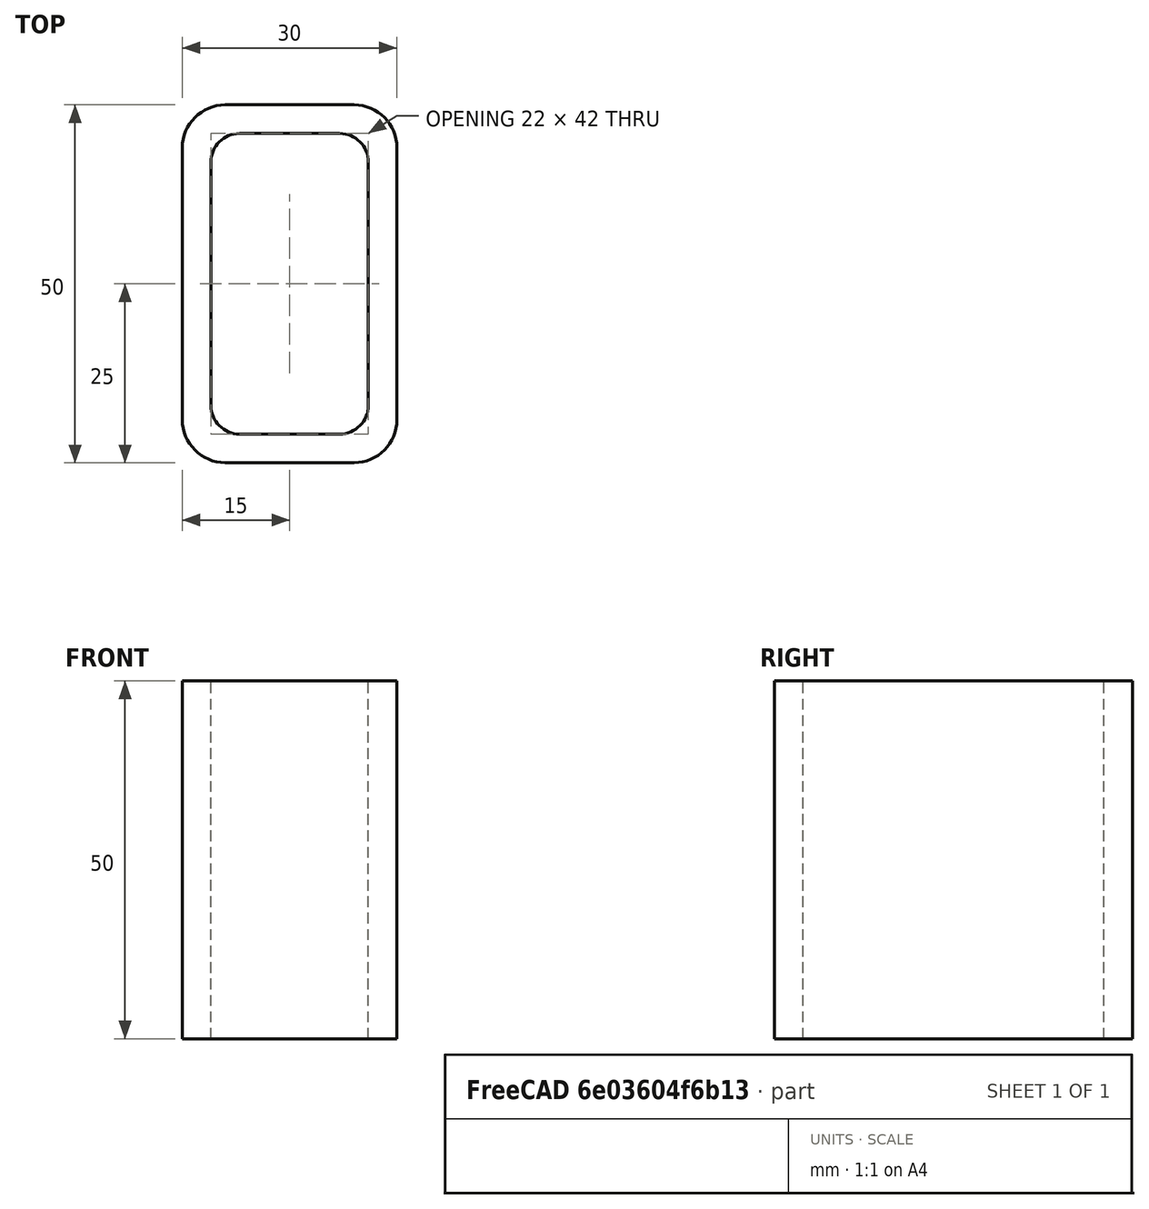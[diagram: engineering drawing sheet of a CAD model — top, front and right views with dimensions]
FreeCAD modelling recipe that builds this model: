
FCSTD DOCUMENT  (FreeCAD 0.15R4671 (Git))
Label: Rectangular hollow section 50x30x4 EN10219 S235JRH
License: All rights reserved
LicenseURL: http://en.wikipedia.org/wiki/All_rights_reserved
objects: Sketcher::SketchObject×1, Part::Extrusion×1
note: 2 computed .brp shape members not serialized (recipe doc carries the construction recipe); baked Part::Feature solids carry a one-line shape summary decoded from their .brp

FEATURE [Sketcher::SketchObject] Sketch
  sketch-geometry (16):
    g0: LineSegment StartX=-7 StartY=21 StartZ=0 EndX=7 EndY=21 EndZ=0
    g1: LineSegment StartX=11 StartY=17 StartZ=0 EndX=11 EndY=-17 EndZ=0
    g2: LineSegment StartX=7 StartY=-21 StartZ=0 EndX=-7 EndY=-21 EndZ=0
    g3: LineSegment StartX=-11 StartY=-17 StartZ=0 EndX=-11 EndY=17 EndZ=0
    g4: LineSegment StartX=-9 StartY=25 StartZ=0 EndX=9 EndY=25 EndZ=0
    g5: LineSegment StartX=15 StartY=19 StartZ=0 EndX=15 EndY=-19 EndZ=0
    g6: LineSegment StartX=9 StartY=-25 StartZ=0 EndX=-9 EndY=-25 EndZ=0
    g7: LineSegment StartX=-15 StartY=-19 StartZ=0 EndX=-15 EndY=19 EndZ=0
    g8: ArcOfCircle CenterX=-7 CenterY=17 CenterZ=0 NormalX=0 NormalY=0 NormalZ=1 Radius=4 StartAngle=1.5708 EndAngle=3.14159
    g9: ArcOfCircle CenterX=7 CenterY=17 CenterZ=0 NormalX=0 NormalY=0 NormalZ=1 Radius=4 StartAngle=0 EndAngle=1.5708
    g10: ArcOfCircle CenterX=7 CenterY=-17 CenterZ=0 NormalX=0 NormalY=0 NormalZ=1 Radius=4 StartAngle=4.71239 EndAngle=6.28319
    g11: ArcOfCircle CenterX=-7 CenterY=-17 CenterZ=0 NormalX=0 NormalY=0 NormalZ=1 Radius=4 StartAngle=3.14159 EndAngle=4.71239
    g12: ArcOfCircle CenterX=9 CenterY=19 CenterZ=0 NormalX=0 NormalY=0 NormalZ=1 Radius=6 StartAngle=0 EndAngle=1.5708
    g13: ArcOfCircle CenterX=9 CenterY=-19 CenterZ=0 NormalX=0 NormalY=0 NormalZ=1 Radius=6 StartAngle=4.71239 EndAngle=6.28319
    g14: ArcOfCircle CenterX=-9 CenterY=-19 CenterZ=0 NormalX=0 NormalY=0 NormalZ=1 Radius=6 StartAngle=3.14159 EndAngle=4.71239
    g15: ArcOfCircle CenterX=-9 CenterY=19 CenterZ=0 NormalX=0 NormalY=0 NormalZ=1 Radius=6 StartAngle=1.5708 EndAngle=3.14159
  constraints (36):
    c: Horizontal(g2)
    c: Vertical(g3)
    c: Horizontal(g6)
    c: Vertical(g7)
    c: Tangent(g3,g8) = 1.5708
    c: Tangent(g0,g8) = 1.5708
    c: Tangent(g0,g9) = 1.5708
    c: Tangent(g1,g9) = 1.5708
    c: Tangent(g1,g10) = 1.5708
    c: Tangent(g2,g10) = 1.5708
    c: Tangent(g2,g11) = 1.5708
    c: Tangent(g3,g11) = 1.5708
    c: Tangent(g4,g12) = 1.5708
    c: Tangent(g5,g12) = 1.5708
    c: Tangent(g5,g13) = 1.5708
    c: Tangent(g6,g13) = 1.5708
    c: Tangent(g6,g14) = 1.5708
    c: Tangent(g7,g14) = 1.5708
    c: Tangent(g7,g15) = 1.5708
    c: Tangent(g4,g15) = 1.5708
    c: Equal(g9,g8)
    c: Equal(g9,g11)
    c: Equal(g9,g10)
    c: Equal(g12,g15)
    c: Equal(g12,g14)
    c: Equal(g12,g13)
    c: Symmetric(g4,g6,g-1)
    c: Symmetric(g7,g5,g-2)
    c: DistanceY(g4,g6) = -50
    c: DistanceX(g7,g5) = 30
    c: Symmetric(g3,g1,g-2)
    c: Symmetric(g0,g2,g-1)
    c: DistanceY(g0,g4) = 4
    c: DistanceX(g5,g1) = -4
    c: Radius(g9) = 4
    c: Radius(g12) = 6
FEATURE [Part::Extrusion] Extrude  label="Rectangular hollow section 50x30x4 EN10219 S235JRH"
  Base = -> Sketch
  Dir = (0,0,50)
  Solid = true
